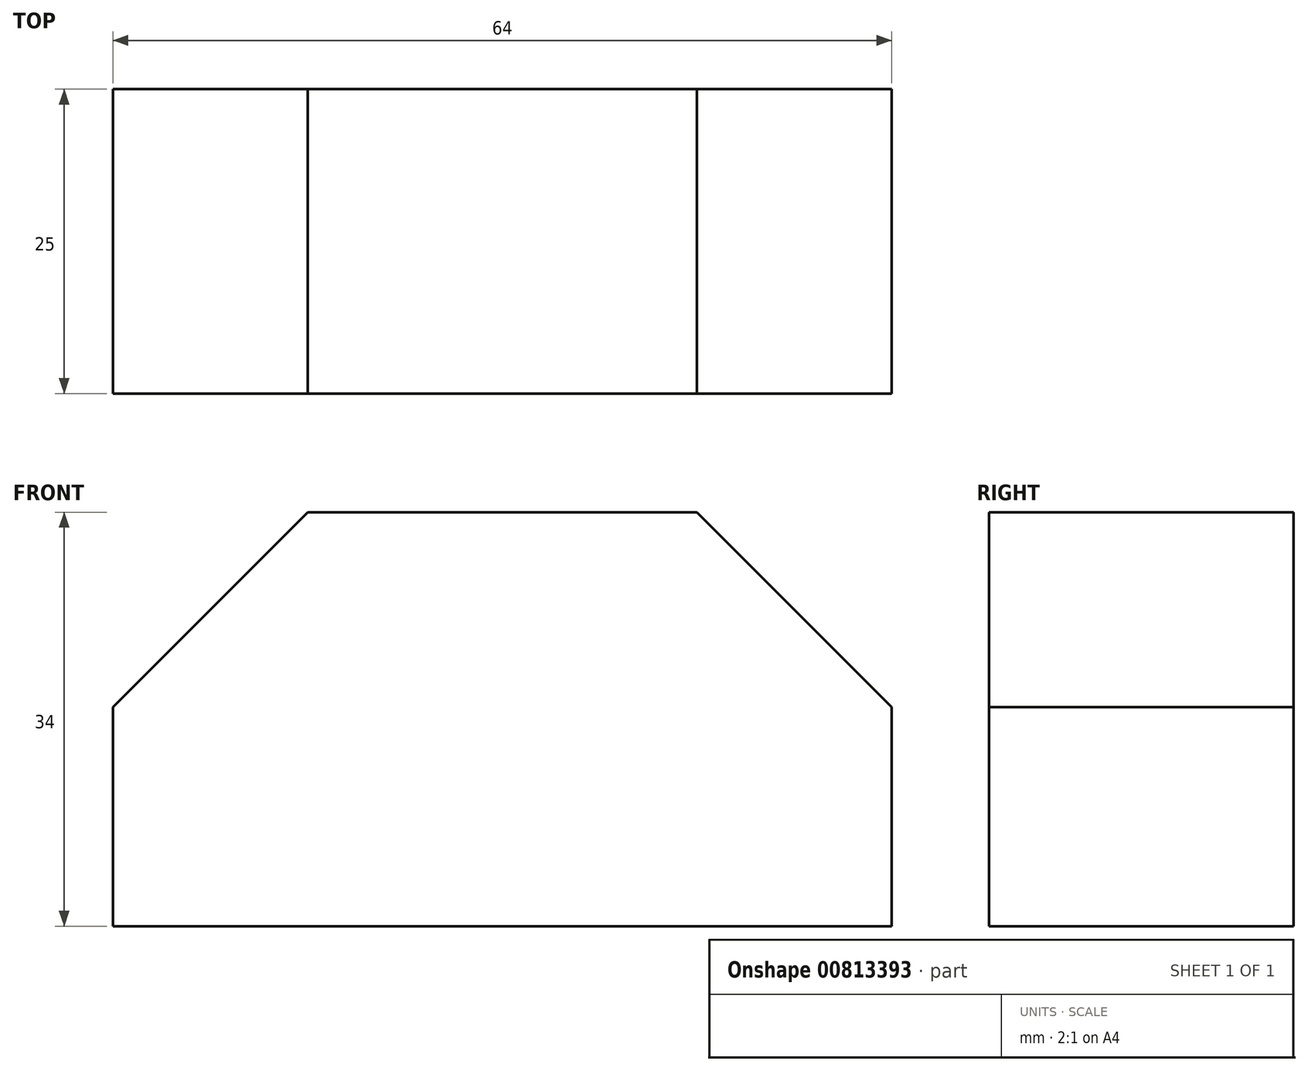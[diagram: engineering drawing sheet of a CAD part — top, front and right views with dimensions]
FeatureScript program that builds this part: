
annotation { "Feature Type Name" : "Feature", "Feature Type Description" : "" }
export const myFeature = defineFeature(function(context is Context, id is Id, definition is map)
    precondition{}
    {
        {
            var Q0;
            Q0=qCreatedBy(makeId("Front.planeOp"),FACE);
            var sketch = newSketch(context, id + "F0", { "sketchPlane" : qUnion([Q0])});
            skLineSegment(sketch, "E0.bottom", {"start": v(0, 0) * mm, "end": v(64, 0) * mm});
            skLineSegment(sketch, "E0.top", {"start": v(0, 34) * mm, "end": v(64, 34) * mm});
            skLineSegment(sketch, "E0.left", {"start": v(0, 0) * mm, "end": v(0, 34) * mm});
            skLineSegment(sketch, "E0.right", {"start": v(64, 0) * mm, "end": v(64, 34) * mm});
            skLineSegment(sketch, "E1", {"start": v(64, 18) * mm, "end": v(48, 34) * mm});
            skLineSegment(sketch, "E2", {"start": v(32, 0) * mm, "end": v(32, 12.44) * mm, "construction": true});
            skLineSegment(sketch, "E3.MirrorCS", {"start": v(0, 18) * mm, "end": v(16, 34) * mm});
            skSolve(sketch);
        }
        {
            var Q0;
            {var subQ1=sQuery(id+"F0.wireOp",EDGE,"E0.bottom");Q0=makeQuery(id+"F0.imprint","IMPRINT",FACE,{"disambiguationData":[TD([[makeQuery(id+"F0.imprint","IMPRINT",EDGE,{"derivedFrom":subQ1}),1.0]])]});}
            extrude(context, id + "F1", {"entities" : qUnion([Q0]), "depth" : 25 * mm, "offsetDistance" : 25 * mm});
        }
    });
